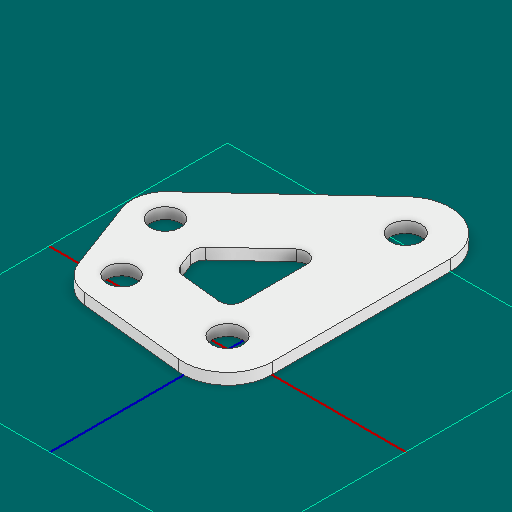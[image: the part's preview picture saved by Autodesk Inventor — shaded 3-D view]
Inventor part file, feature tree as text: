
AUTODESK INVENTOR PART (.ipt)
format: ipt  version: 2025 (Build 290162000, 162)  size: 139,264 bytes
history: native  units: in
note: dims shown in document units (in); Inventor stores cm internally (conversion verified against a paired STEP export)
features: other x3, extrude x1, sketch x1
ambient origin geometry x8: Origin, YZ Plane, XZ Plane, XY Plane, X Axis, Y Axis, Z Axis, Center Point
bodies: Solid1 (feature_tree)
feature tree (5):
  other  "Blocks"
  extrude  "Extrusion1"  Depth=0.375in
  sketch  "Sketch1"  dims[d0=0.165in d1=0.5in d2=0.5in d3=0.375in d4=0.375in d5=0.0625in d6=0.0625in d7=0.0in]
  other  "main"
  other  "main:1"
